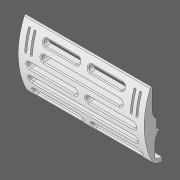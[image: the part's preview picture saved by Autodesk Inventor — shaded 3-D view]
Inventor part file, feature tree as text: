
AUTODESK INVENTOR PART (.ipt)
format: ipt  version: 2020 (Build 240168000, 168)  size: 622,592 bytes
history: native  units: in
note: dims shown in document units (in); Inventor stores cm internally (conversion verified against a paired STEP export)
features: extrude x3, fillet x2, other x2, sketch x2
ambient origin geometry x8: Origin, YZ Plane, XZ Plane, XY Plane, X Axis, Y Axis, Z Axis, Center Point
bodies: Solid1 (feature_tree)
feature tree (9):
  extrude  "Slots"  Depth=0.0591in
  extrude  "Extrusion3"  Depth=0.0197in
  fillet  "Fillet2"  Radius=0.0197in
  extrude  "Extrusion4"  Depth=0.1181in
  fillet  "Fillet3"  Radius=0.2362in
  other  "Profile"
  other  "Slot Sketch"
  sketch  "Sketch3"  dims[d0=7.0866in d1=0.0in d3=0.0591in]
  sketch  "Sketch4"  dims[d5=0.5906in d14=0.0197in d15=0.0197in d16=0.1181in d17=0.2362in d18=0.1181in d19=0.3056in d20=0.2362in d21=0.5978in d22=0.0in d26=0.0197in d27=0.0197in d28=0.1181in d29=0.2362in d30=0.1181in d31=0.0079in d35=6.6142in d36=0.0197in d37=0.0197in d38=0.1181in d39=0.2362in d40=0.1181in d41=0.0079in d45=3.3071in d48=3.5433in d50=0.7874in d51=1.1811in d52=0.1181in d53=0.4724in d54=0.0in d55=0.0in d56=0.1969in d57=0.1969in d58=0.0591in d59=0.1575in d62=4.252in d71=0.0in d72=0.0in d83=3.5433in d85=0.2953in d86=0.6299in d87=0.3937in d88=0.3937in d89=0.3937in d92=0.6299in d93=0.0591in d95=0.3937in d96=0.6299in d97=0.3937in d98=4.252in d99=0.3937in d100=4.3307in d114=0.7874in d115=0.3056in d122=0.2362in d124=0.2362in d127=0.1181in d129=0.7874in d130=1.634in d131=0.4724in d133=0.7874in d134=0.2362in d135=0.1181in d136=0.3937in]
